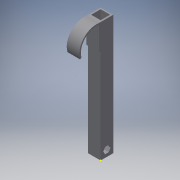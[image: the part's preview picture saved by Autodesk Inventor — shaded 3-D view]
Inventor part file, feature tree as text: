
AUTODESK INVENTOR PART (.ipt)
format: ipt  version: 2016 (Build 200138000, 138)  size: 178,688 bytes
history: native  units: in
note: dims shown in document units (in); Inventor stores cm internally (conversion verified against a paired STEP export)
features: sketch x6, extrude x5
ambient origin geometry x8: Origin, YZ Plane, XZ Plane, XY Plane, X Axis, Y Axis, Z Axis, Center Point
bodies: Solid1 (feature_tree)
feature tree (11):
  extrude  "Extrusion1"  Depth=1.0in
  extrude  "Extrusion2"  Depth=0.5in
  extrude  "Extrusion3"  Depth=0.125in
  sketch  "Sketch4"  dims[d8=9.0in d9=0.0in d11=2.0in]
  extrude  "Extrusion4"  Depth=2.0in
  extrude  "Extrusion5"  Depth=0.125in
  sketch  "Sketch1"  dims[d0=9.5in d1=1.0in]
  sketch  "Sketch2"  dims[d3=0.5in d4=0.5in]
  sketch  "Sketch3"  dims[d5=1.0in d6=0.0in d7=0.125in]
  sketch  "Sketch5"  dims[d13=0.125in d15=0.125in]
  sketch  "Sketch6"  dims[d16=1.0in d17=0.0in d18=1.75in d19=1.5in d20=0.125in d21=0.125in d22=1.0in d23=0.0in d25=0.5in d26=0.5in d27=0.5in d28=1.0in d29=0.0in]
